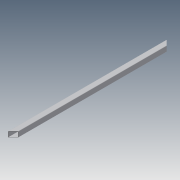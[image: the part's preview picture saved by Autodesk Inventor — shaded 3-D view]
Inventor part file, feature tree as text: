
AUTODESK INVENTOR PART (.ipt)
format: ipt  version: 2014 (Build 180170000, 170)  size: 107,520 bytes
history: native  units: in
note: dims shown in document units (in); Inventor stores cm internally (conversion verified against a paired STEP export)
features: extrude x2, sketch x2
ambient origin geometry x8: Origin, YZ Plane, XZ Plane, XY Plane, X Axis, Y Axis, Z Axis, Center Point
bodies: Solid1 (feature_tree)
feature tree (4):
  extrude  "Extrusion1"  Depth=1.0in
  extrude  "Extrusion2"  Depth=0.063in
  sketch  "Sketch1"  dims[d0=1.0in d1=1.0in]
  sketch  "Sketch2"  dims[d2=0.07in d3=0.063in d4=29.5in d5=0.0in d7=45.0deg d9=45.0deg d10=1.0in d11=0.0in]
